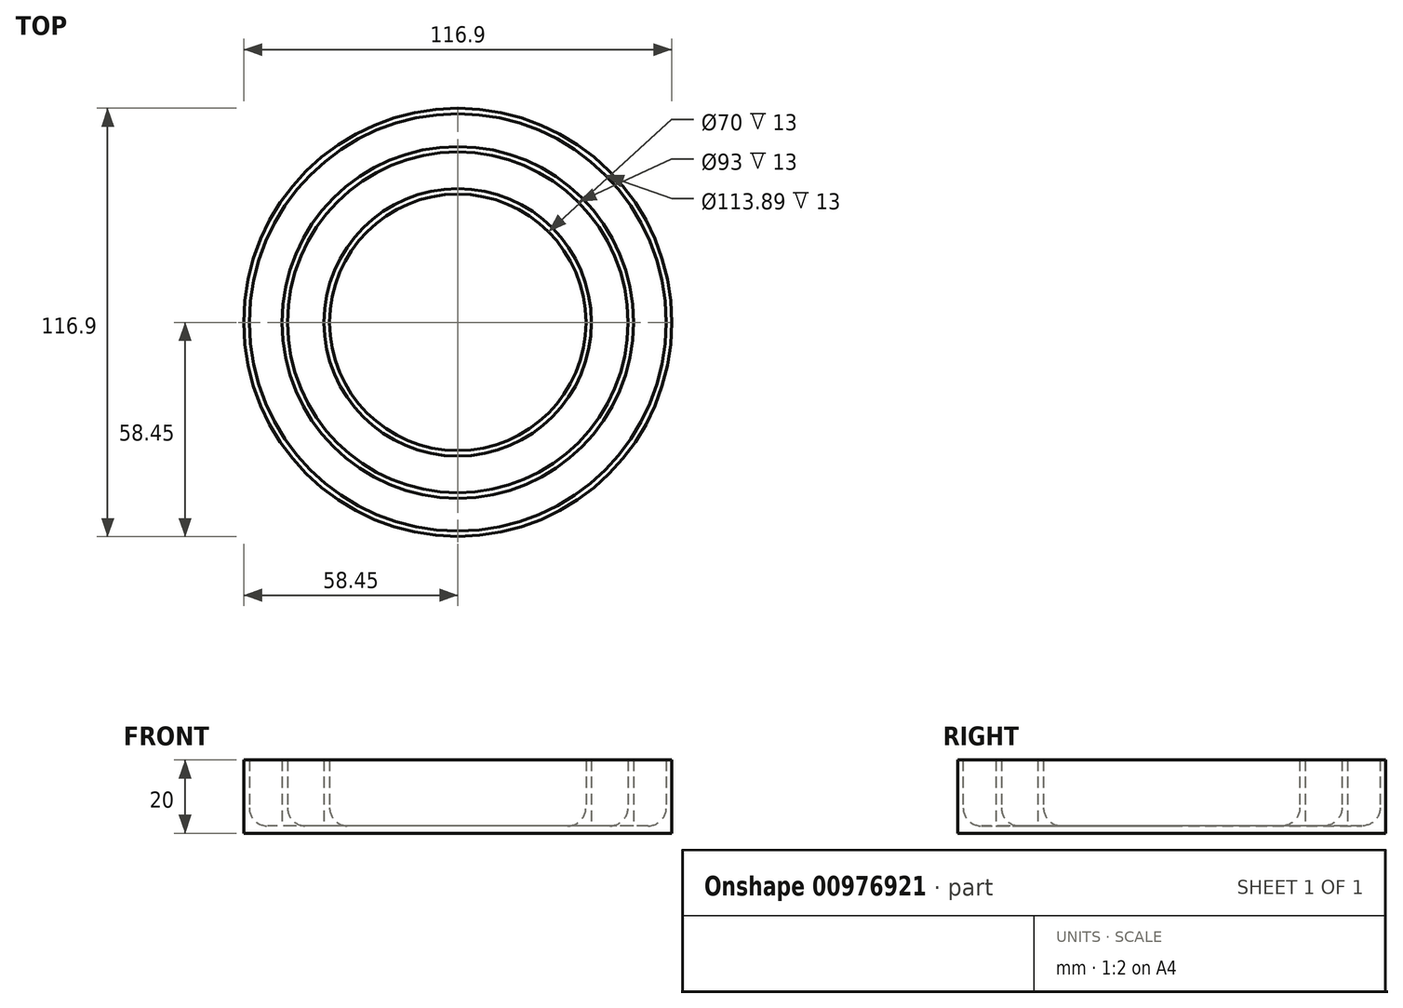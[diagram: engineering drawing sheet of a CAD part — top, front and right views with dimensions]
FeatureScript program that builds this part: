
annotation { "Feature Type Name" : "Feature", "Feature Type Description" : "" }
export const myFeature = defineFeature(function(context is Context, id is Id, definition is map)
    precondition{}
    {
        {
            var Q0;
            Q0=qCreatedBy(makeId("Top.planeOp"),FACE);
            var sketch = newSketch(context, id + "F0", { "sketchPlane" : qUnion([Q0])});
            skCircle(sketch, "E0", {"center": v(0, 0) * mm, "radius": 35 * mm});
            skCircle(sketch, "E1", {"center": v(0, 0) * mm, "radius": 36.5 * mm});
            skCircle(sketch, "E2", {"center": v(0, 0) * mm, "radius": 46.5 * mm});
            skCircle(sketch, "E3", {"center": v(0, 0) * mm, "radius": 58.45 * mm});
            skCircle(sketch, "E4", {"center": v(0, 0) * mm, "radius": 48 * mm});
            skCircle(sketch, "E5", {"center": v(0, 0) * mm, "radius": 56.95 * mm});
            skSolve(sketch);
        }
        {
            var Q0;
            Q0=makeQuery(id+"F0.imprint","IMPRINT",FACE,{"disambiguationData":[TD([[makeQuery(id+"F0.imprint","IMPRINT",EDGE,{"derivedFrom":sQuery(id+"F0.wireOp",EDGE,"E3")}),1.0]])]});
            var Q1;
            Q1=makeQuery(id+"F0.imprint","IMPRINT",FACE,{"disambiguationData":[TD([[makeQuery(id+"F0.imprint","IMPRINT",EDGE,{"derivedFrom":sQuery(id+"F0.wireOp",EDGE,"E4")}),-1.0]])]});
            var Q2;
            Q2=makeQuery(id+"F0.imprint","IMPRINT",FACE,{"disambiguationData":[TD([[makeQuery(id+"F0.imprint","IMPRINT",EDGE,{"derivedFrom":sQuery(id+"F0.wireOp",EDGE,"E2")}),-1.0]])]});
            var Q3;
            Q3=makeQuery(id+"F0.imprint","IMPRINT",FACE,{"disambiguationData":[TD([[makeQuery(id+"F0.imprint","IMPRINT",EDGE,{"derivedFrom":sQuery(id+"F0.wireOp",EDGE,"E1")}),-1.0]])]});
            var Q4;
            Q4=makeQuery(id+"F0.imprint","IMPRINT",FACE,{"disambiguationData":[TD([[makeQuery(id+"F0.imprint","IMPRINT",EDGE,{"derivedFrom":sQuery(id+"F0.wireOp",EDGE,"E0")}),-1.0]])]});
            var Q5;
            Q5=makeQuery(id+"F0.imprint","IMPRINT",FACE,{"disambiguationData":[TD([[makeQuery(id+"F0.imprint","IMPRINT",EDGE,{"derivedFrom":sQuery(id+"F0.wireOp",EDGE,"E0")}),1.0]])]});
            extrude(context, id + "F1", {"entities" : qUnion([Q0, Q1, Q2, Q3, Q4, Q5]), "depth" : 2 * mm, "offsetDistance" : 25 * mm});
        }
        {
            var Q0;
            Q0=makeQuery(id+"F0.imprint","IMPRINT",FACE,{"disambiguationData":[TD([[makeQuery(id+"F0.imprint","IMPRINT",EDGE,{"derivedFrom":sQuery(id+"F0.wireOp",EDGE,"E2")}),-1.0]])]});
            var Q1;
            Q1=makeQuery(id+"F0.imprint","IMPRINT",FACE,{"disambiguationData":[TD([[makeQuery(id+"F0.imprint","IMPRINT",EDGE,{"derivedFrom":sQuery(id+"F0.wireOp",EDGE,"E0")}),-1.0]])]});
            var Q2;
            Q2=makeQuery(id+"F0.imprint","IMPRINT",FACE,{"disambiguationData":[TD([[makeQuery(id+"F0.imprint","IMPRINT",EDGE,{"derivedFrom":sQuery(id+"F0.wireOp",EDGE,"E3")}),1.0]])]});
            extrude(context, id + "F2", {"entities" : qUnion([Q0, Q1, Q2]), "operationType" : NewBodyOperationType.ADD, "depth" : 20 * mm, "offsetDistance" : 25 * mm});
        }
        {
            var Q0;
            Q0=makeQuery(id+"F2.boolean.opBoolean","INTERSECT",EDGE,{"derivedFrom":[makeQuery(id+"F1.opExtrude","CAP_FACE",FACE,{"disambiguationData":[OSD([sQuery(id+"F0.wireOp",EDGE,"E3")])],"isStart":false}),makeQuery(id+"F2.opExtrude","SWEPT_FACE",FACE,{"disambiguationData":[OSD([sQuery(id+"F0.wireOp",EDGE,"E0")])]})]});
            var Q1;
            Q1=makeQuery(id+"F2.boolean.opBoolean","INTERSECT",EDGE,{"derivedFrom":[makeQuery(id+"F1.opExtrude","CAP_FACE",FACE,{"disambiguationData":[OSD([sQuery(id+"F0.wireOp",EDGE,"E3")])],"isStart":false}),makeQuery(id+"F2.opExtrude","SWEPT_FACE",FACE,{"disambiguationData":[OSD([sQuery(id+"F0.wireOp",EDGE,"E2")])]})]});
            var Q2;
            Q2=makeQuery(id+"F2.boolean.opBoolean","INTERSECT",EDGE,{"derivedFrom":[makeQuery(id+"F1.opExtrude","CAP_FACE",FACE,{"disambiguationData":[OSD([sQuery(id+"F0.wireOp",EDGE,"E3")])],"isStart":false}),makeQuery(id+"F2.opExtrude","SWEPT_FACE",FACE,{"disambiguationData":[OSD([sQuery(id+"F0.wireOp",EDGE,"E5")])]})]});
            fillet(context, id + "F3", {"entities" : qUnion([Q0, Q1, Q2]), "radius" : 5 * mm, "tangentPropagation" : true, "allowEdgeOverflow" : false});
        }
    });
